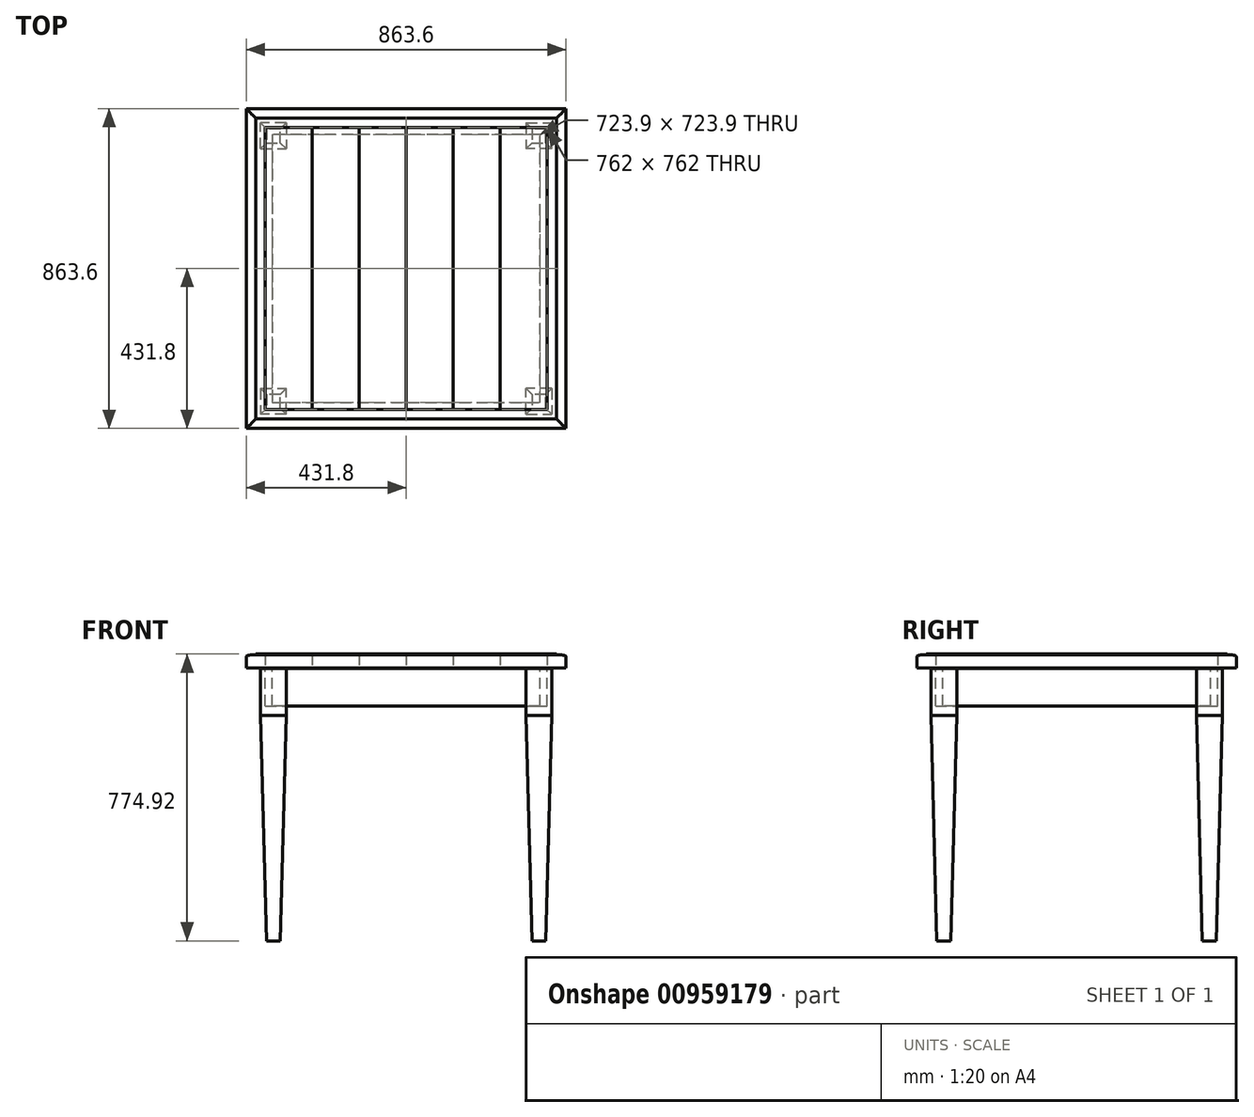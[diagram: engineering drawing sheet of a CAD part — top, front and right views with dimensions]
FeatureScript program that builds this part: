
annotation { "Feature Type Name" : "Feature", "Feature Type Description" : "" }
export const myFeature = defineFeature(function(context is Context, id is Id, definition is map)
    precondition{}
    {
        {
            var Q0;
            Q0=qCreatedBy(makeId("Front.planeOp"),FACE);
            var sketch = newSketch(context, id + "F0", { "sketchPlane" : qUnion([Q0])});
            skLineSegment(sketch, "E0", {"start": v(0, 0) * mm, "end": v(0, -870.05) * mm, "construction": true});
            skSolve(sketch);
        }
        {
            var Q0;
            Q0=qCreatedBy(makeId("Top.planeOp"),FACE);
            var sketch = newSketch(context, id + "F1", { "sketchPlane" : qUnion([Q0])});
            skLineSegment(sketch, "E1.0", {"start": v(323.85, -393.7) * mm, "end": v(393.7, -393.7) * mm});
            skLineSegment(sketch, "E1.3", {"start": v(393.7, -323.85) * mm, "end": v(393.7, -393.7) * mm});
            skLineSegment(sketch, "E2.bottom", {"start": v(393.7, -393.7) * mm, "end": v(323.85, -393.7) * mm});
            skLineSegment(sketch, "E2.top", {"start": v(393.7, -323.85) * mm, "end": v(323.85, -323.85) * mm});
            skLineSegment(sketch, "E2.left", {"start": v(393.7, -393.7) * mm, "end": v(393.7, -323.85) * mm});
            skLineSegment(sketch, "E2.right", {"start": v(323.85, -393.7) * mm, "end": v(323.85, -323.85) * mm});
            skPoint(sketch, "E3.0.end.orphan", {"position": v(431.8, -431.8) * mm});
            skPoint(sketch, "E3.0.start.orphan", {"position": v(-431.8, -431.8) * mm});
            skPoint(sketch, "E4.0.start.orphan", {"position": v(431.8, 431.8) * mm});
            skPoint(sketch, "E5.0.start.orphan", {"position": v(-431.8, 431.8) * mm});
            skLineSegment(sketch, "E6.bottom", {"start": v(431.8, -431.8) * mm, "end": v(-431.8, -431.8) * mm, "construction": true});
            skLineSegment(sketch, "E6.top", {"start": v(431.8, 431.8) * mm, "end": v(-431.8, 431.8) * mm, "construction": true});
            skLineSegment(sketch, "E6.left", {"start": v(431.8, -431.8) * mm, "end": v(431.8, 431.8) * mm, "construction": true});
            skLineSegment(sketch, "E6.right", {"start": v(-431.8, -431.8) * mm, "end": v(-431.8, 431.8) * mm, "construction": true});
            skPoint(sketch, "E6.middle", {"position": v(0, 0) * mm});
            skSolve(sketch);
        }
        {
            var Q0;
            Q0=qSketchRegion(id+"F1",true);
            extrude(context, id + "F2", {"entities" : qUnion([Q0]), "oppositeDirection" : true, "depth" : 127 * mm, "offsetDistance" : 25.4 * mm});
        }
        {
            var Q0;
            Q0=makeQuery(id+"F2.opExtrude","SWEPT_BODY",BODY,{"disambiguationData":[OSD([sQuery(id+"F1.wireOp",EDGE,"E2.bottom"),sQuery(id+"F1.wireOp",EDGE,"E2.top"),sQuery(id+"F1.wireOp",EDGE,"E2.left"),sQuery(id+"F1.wireOp",EDGE,"E2.right")])]});
            var Q1;
            Q1=sQuery(id+"F0.wireOp",EDGE,"E0");
            circularPattern(context, id + "F3", {"entities" : qUnion([Q0]), "axis" : qUnion([Q1]), "angle" : 360 * degree, "instanceCount" : 4, "equalSpace" : true});
        }
        {
            var Q0;
            Q0=qCreatedBy(makeId("Top.planeOp"),FACE);
            var sketch = newSketch(context, id + "F4", { "sketchPlane" : qUnion([Q0])});
            skLineSegment(sketch, "E7.bottom", {"start": v(-381, 381) * mm, "end": v(381, 381) * mm});
            skLineSegment(sketch, "E7.top", {"start": v(-381, -381) * mm, "end": v(381, -381) * mm});
            skLineSegment(sketch, "E7.left", {"start": v(-381, 381) * mm, "end": v(-381, -381) * mm});
            skLineSegment(sketch, "E7.right", {"start": v(381, 381) * mm, "end": v(381, -381) * mm});
            skPoint(sketch, "E7.middle", {"position": v(0, 0) * mm});
            skLineSegment(sketch, "E8", {"start": v(-254, 381) * mm, "end": v(-254, -381) * mm});
            skLineSegment(sketch, "E9.1.0.0", {"start": v(-127, 381) * mm, "end": v(-127, -381) * mm});
            skLineSegment(sketch, "E9.2.0.0", {"start": v(0, 381) * mm, "end": v(0, -381) * mm});
            skLineSegment(sketch, "E9.3.0.0", {"start": v(127, 381) * mm, "end": v(127, -381) * mm});
            skLineSegment(sketch, "E9.4.0.0", {"start": v(254, 381) * mm, "end": v(254, -381) * mm});
            skLineSegment(sketch, "E9.direction1", {"start": v(-254, -381) * mm, "end": v(-127, -381) * mm, "construction": true});
            skSolve(sketch);
        }
        {
            var Q0;
            {var subQ0=sQuery(id+"F4.wireOp",EDGE,"E7.left");Q0=makeQuery(id+"F4.imprint","IMPRINT",FACE,{"disambiguationData":[TD([[makeQuery(id+"F4.imprint","IMPRINT",EDGE,{"derivedFrom":subQ0}),1.0]])]});}
            var Q1;
            {var subQ0=sQuery(id+"F4.wireOp",EDGE,"E9.1.0.0");Q1=makeQuery(id+"F4.imprint","IMPRINT",FACE,{"disambiguationData":[TD([[makeQuery(id+"F4.imprint","IMPRINT",EDGE,{"derivedFrom":subQ0}),1.0]])]});}
            var Q2;
            {var subQ0=sQuery(id+"F4.wireOp",EDGE,"E9.3.0.0");Q2=makeQuery(id+"F4.imprint","IMPRINT",FACE,{"disambiguationData":[TD([[makeQuery(id+"F4.imprint","IMPRINT",EDGE,{"derivedFrom":subQ0}),1.0]])]});}
            extrude(context, id + "F5", {"entities" : qUnion([Q0, Q1, Q2]), "depth" : 38.1 * mm, "offsetDistance" : 25.4 * mm});
        }
        {
            var Q0;
            {var subQ0=sQuery(id+"F4.wireOp",EDGE,"E8");Q0=makeQuery(id+"F4.imprint","IMPRINT",FACE,{"disambiguationData":[TD([[makeQuery(id+"F4.imprint","IMPRINT",EDGE,{"derivedFrom":subQ0}),1.0]])]});}
            var Q1;
            {var subQ0=sQuery(id+"F4.wireOp",EDGE,"E9.2.0.0");Q1=makeQuery(id+"F4.imprint","IMPRINT",FACE,{"disambiguationData":[TD([[makeQuery(id+"F4.imprint","IMPRINT",EDGE,{"derivedFrom":subQ0}),1.0]])]});}
            var Q2;
            {var subQ0=sQuery(id+"F4.wireOp",EDGE,"E7.right");Q2=makeQuery(id+"F4.imprint","IMPRINT",FACE,{"disambiguationData":[TD([[makeQuery(id+"F4.imprint","IMPRINT",EDGE,{"derivedFrom":subQ0}),-1.0]])]});}
            extrude(context, id + "F6", {"entities" : qUnion([Q0, Q1, Q2]), "depth" : 38.13 * mm, "offsetDistance" : 25.4 * mm});
        }
        {
            var Q0;
            Q0=qCreatedBy(makeId("Top.planeOp"),FACE);
            var sketch = newSketch(context, id + "F7", { "sketchPlane" : qUnion([Q0])});
            skLineSegment(sketch, "E10.bottom", {"start": v(-381, 381) * mm, "end": v(381, 381) * mm});
            skLineSegment(sketch, "E10.top", {"start": v(-381, -381) * mm, "end": v(381, -381) * mm});
            skLineSegment(sketch, "E10.left", {"start": v(-381, 381) * mm, "end": v(-381, -381) * mm});
            skLineSegment(sketch, "E10.right", {"start": v(381, 381) * mm, "end": v(381, -381) * mm});
            skPoint(sketch, "E10.middle", {"position": v(0, 0) * mm});
            skSolve(sketch);
        }
        {
            var Q0;
            Q0 = qSketchRegion(id + "F7", true);
            extrude(context, id + "F8", {"entities" : qUnion([Q0]), "depth" : 38.1 * mm, "offsetDistance" : 25.4 * mm});
        }
        {
            var Q0;
            Q0=qCreatedBy(makeId("Right.planeOp"),FACE);
            var sketch = newSketch(context, id + "F9", { "sketchPlane" : qUnion([Q0])});
            skLineSegment(sketch, "E11", {"start": v(-381, 0.22) * mm, "end": v(-431.8, 0.22) * mm});
            skLineSegment(sketch, "E12", {"start": v(-206.4, -341.69) * mm, "end": v(-206.4, -341.69) * mm});
            skLineSegment(sketch, "E13", {"start": v(-200.05, -335.34) * mm, "end": v(-200.05, -335.34) * mm});
            skLineSegment(sketch, "E14", {"start": v(-406.4, 38.32) * mm, "end": v(-381, 38.32) * mm});
            skPoint(sketch, "E15.visualSharp", {"position": v(-464.21, 38.32) * mm});
            skPoint(sketch, "E16.visualSharp", {"position": v(-464.21, 6.35) * mm});
            skLineSegment(sketch, "E17", {"start": v(-381, 38.32) * mm, "end": v(-381, 0.22) * mm});
            skLineSegment(sketch, "E18", {"start": v(-406.4, 38.32) * mm, "end": v(-406.4, 36.74) * mm});
            skLineSegment(sketch, "E19", {"start": v(-431.8, 0.22) * mm, "end": v(-431.8, 28.8) * mm});
            skFitSpline(sketch, "E20", {"points": [v(-406.4, 36.74) * mm, v(-426.46, 35.05) * mm, v(-431.8, 28.8) * mm], "startDerivative": vector(-24.81, 0) * mm, "endDerivative": vector(0, -34.47) * mm});
            skLineSegment(sketch, "E21", {"start": v(-426.12, 36.74) * mm, "end": v(-406.4, 36.74) * mm, "construction": true});
            skSolve(sketch);
        }
        {
            var Q0;
            Q0=makeQuery(id+"F9.imprint","IMPRINT",FACE,{"disambiguationData":[TD([[makeQuery(id+"F9.imprint","IMPRINT",EDGE,{"derivedFrom":sQuery(id+"F9.wireOp",EDGE,"E11")}),-1.0]])]});
            var Q1;
            Q1=makeQuery(id+"F8.opExtrude","CAP_EDGE",EDGE,{"disambiguationData":[OSD([sQuery(id+"F7.wireOp",EDGE,"E10.top")])],"isStart":true});
            var Q2;
            Q2=makeQuery(id+"F8.opExtrude","CAP_EDGE",EDGE,{"disambiguationData":[OSD([sQuery(id+"F7.wireOp",EDGE,"E10.right")])],"isStart":true});
            var Q3;
            Q3=makeQuery(id+"F8.opExtrude","CAP_EDGE",EDGE,{"disambiguationData":[OSD([sQuery(id+"F7.wireOp",EDGE,"E10.bottom")])],"isStart":true});
            var Q4;
            Q4=makeQuery(id+"F8.opExtrude","CAP_EDGE",EDGE,{"disambiguationData":[OSD([sQuery(id+"F7.wireOp",EDGE,"E10.left")])],"isStart":true});
            sweep(context, id + "F10", {"profiles" : qUnion([Q0]), "path" : qUnion([Q1, Q2, Q3, Q4])});
        }
        {
            var Q0;
            Q0=qCreatedBy(makeId("Top.planeOp"),FACE);
            var sketch = newSketch(context, id + "F11", { "sketchPlane" : qUnion([Q0])});
            skLineSegment(sketch, "E22.bottom", {"start": v(-381, -381) * mm, "end": v(381, -381) * mm});
            skLineSegment(sketch, "E22.top", {"start": v(-381, 381) * mm, "end": v(381, 381) * mm});
            skLineSegment(sketch, "E22.left", {"start": v(-381, -381) * mm, "end": v(-381, 381) * mm});
            skLineSegment(sketch, "E22.right", {"start": v(381, -381) * mm, "end": v(381, 381) * mm});
            skPoint(sketch, "E22.middle", {"position": v(0, 0) * mm});
            skLineSegment(sketch, "E23.0", {"start": v(-361.95, 361.95) * mm, "end": v(-361.95, -361.95) * mm});
            skLineSegment(sketch, "E23.1", {"start": v(361.95, 361.95) * mm, "end": v(-361.95, 361.95) * mm});
            skLineSegment(sketch, "E23.2", {"start": v(361.95, -361.95) * mm, "end": v(361.95, 361.95) * mm});
            skLineSegment(sketch, "E23.3", {"start": v(-361.95, -361.95) * mm, "end": v(361.95, -361.95) * mm});
            skSolve(sketch);
        }
        {
            var Q0;
            Q0 = qSketchRegion(id + "F11", true);
            extrude(context, id + "F12", {"entities" : qUnion([Q0]), "oppositeDirection" : true, "depth" : 101.6 * mm, "offsetDistance" : 25.4 * mm});
        }
        {
            var Q0;
            Q0=makeQuery(id+"F2.opExtrude","CAP_FACE",FACE,{"disambiguationData":[OSD([sQuery(id+"F1.wireOp",EDGE,"E2.bottom"),sQuery(id+"F1.wireOp",EDGE,"E2.top"),sQuery(id+"F1.wireOp",EDGE,"E2.left"),sQuery(id+"F1.wireOp",EDGE,"E2.right")])],"isStart":false});
            var sketch = newSketch(context, id + "F13", { "sketchPlane" : qUnion([Q0])});
            skLineSegment(sketch, "E24.0.0", {"start": v(393.7, 323.85) * mm, "end": v(393.7, 393.7) * mm});
            skLineSegment(sketch, "E24.0.1", {"start": v(393.7, 393.7) * mm, "end": v(323.85, 393.7) * mm});
            skLineSegment(sketch, "E24.0.2", {"start": v(323.85, 393.7) * mm, "end": v(323.85, 323.85) * mm});
            skLineSegment(sketch, "E24.0.3", {"start": v(323.85, 323.85) * mm, "end": v(393.7, 323.85) * mm});
            skSolve(sketch);
        }
        {
            var Q0;
            Q0 = qSketchRegion(id + "F13", true);
            extrude(context, id + "F14", {"entities" : qUnion([Q0]), "operationType" : NewBodyOperationType.ADD, "depth" : 609.6 * mm, "offsetDistance" : 25.4 * mm, "hasDraft" : true, "draftAngle" : 1.5 * degree, "draftPullDirection" : true});
        }
        {
            var Q0;
            Q0=makeQuery(id+"F2.opExtrude","SWEPT_BODY",BODY,{"disambiguationData":[OSD([sQuery(id+"F1.wireOp",EDGE,"E2.bottom"),sQuery(id+"F1.wireOp",EDGE,"E2.top"),sQuery(id+"F1.wireOp",EDGE,"E2.left"),sQuery(id+"F1.wireOp",EDGE,"E2.right")])]});
            var Q1;
            Q1=sQuery(id+"F0.wireOp",EDGE,"E0");
            circularPattern(context, id + "F15", {"entities" : qUnion([Q0]), "axis" : qUnion([Q1]), "angle" : 360 * degree, "instanceCount" : 4, "equalSpace" : true});
        }
    });
